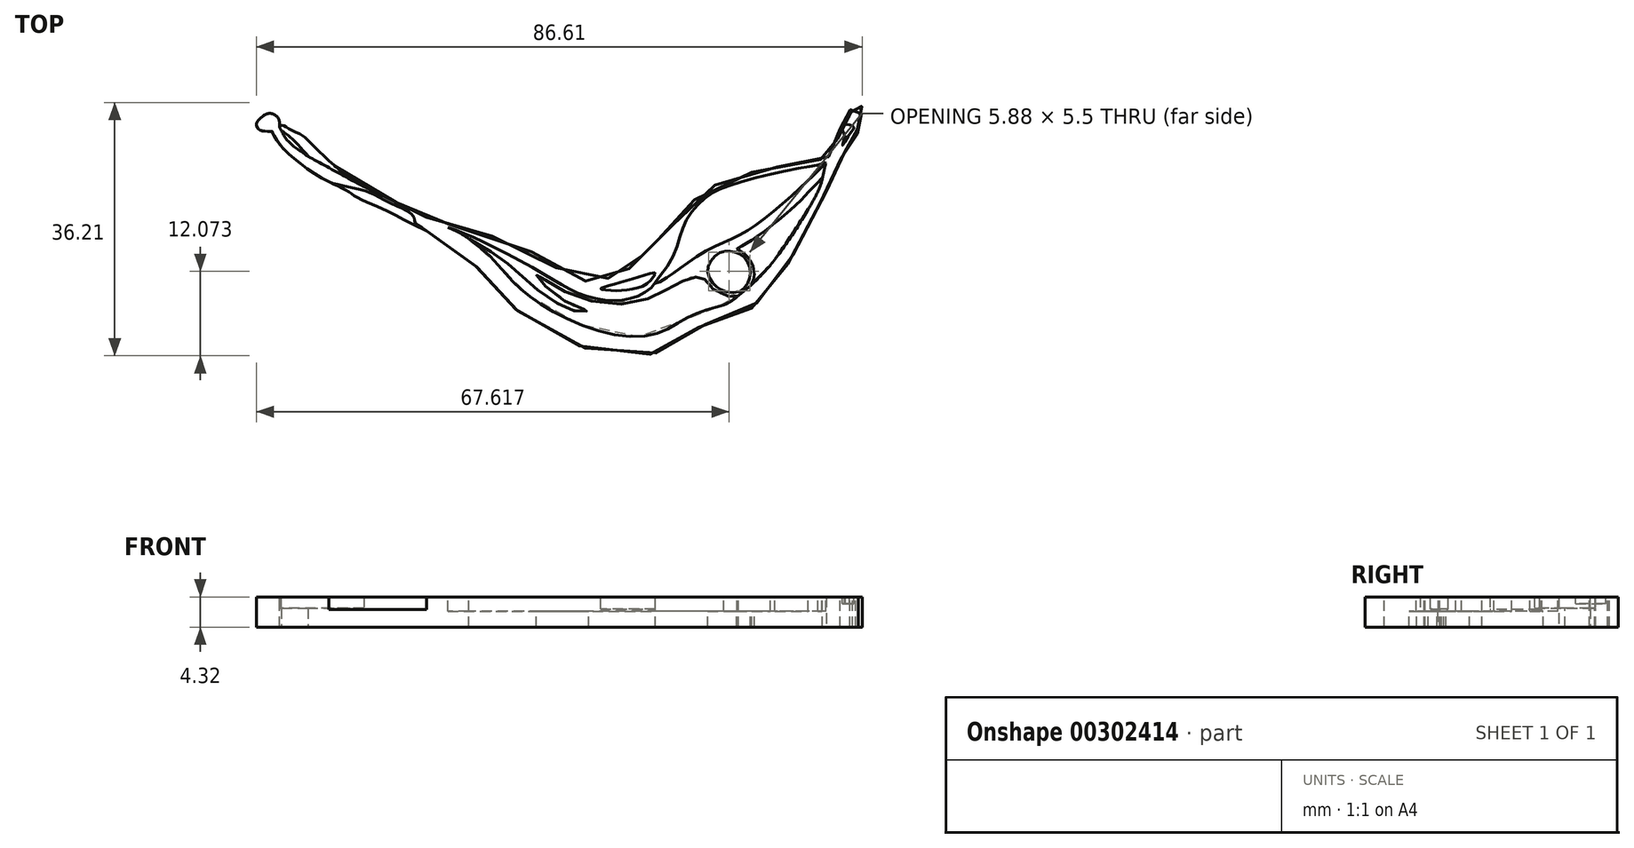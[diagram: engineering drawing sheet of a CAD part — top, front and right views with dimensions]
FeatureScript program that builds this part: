
annotation { "Feature Type Name" : "Feature", "Feature Type Description" : "" }
export const myFeature = defineFeature(function(context is Context, id is Id, definition is map)
    precondition{}
    {
        {
            var Q0;
            Q0=qCreatedBy(makeId("Top.planeOp"),FACE);
            var sketch = newSketch(context, id + "F0", { "sketchPlane" : qUnion([Q0])});
            skFitSpline(sketch, "E0", {"points": [v(-43.46, 14.38) * mm, v(-44.23, 13.82) * mm, v(-44.8, 13.18) * mm, v(-44.82, 12.68) * mm, v(-44.36, 12.07) * mm, v(-43.25, 11.92) * mm, v(-42.68, 11.9) * mm, v(-42.57, 11.9) * mm, v(-42.53, 11.75) * mm, v(-41.7, 10.3) * mm, v(-39.3, 7.87) * mm, v(-34.59, 4.74) * mm, v(-31.85, 3.4) * mm, v(-30.37, 2.4) * mm, v(-26.53, 0.67) * mm, v(-23.64, -0.81) * mm, v(-20.37, -2.4) * mm, v(-17.35, -4.13) * mm, v(-13.45, -7.38) * mm, v(-9.8, -11.5) * mm, v(-7.92, -13.38) * mm, v(-5.1, -15.68) * mm, v(2.66, -19.24) * mm, v(8.89, -20.2) * mm, v(13.19, -19.5) * mm, v(16.5, -17.42) * mm, v(19.24, -15.76) * mm, v(23.96, -14.69) * mm, v(26.11, -13.28) * mm, v(28.6, -10.38) * mm, v(30.9, -7.42) * mm, v(33.51, -2.7) * mm, v(36.14, 2.38) * mm, v(38, 6.37) * mm, v(38.5, 7.84) * mm, v(39, 8.38) * mm, v(39.55, 9.56) * mm, v(40.04, 10.09) * mm, v(40.35, 11.03) * mm, v(41.15, 11.69) * mm, v(41.15, 11.97) * mm, v(40.9, 12.98) * mm, v(40.84, 13.54) * mm, v(40.94, 13.74) * mm, v(41.47, 14.13) * mm, v(41.74, 14.96) * mm, v(41.54, 15.76) * mm, v(40.73, 16) * mm, v(40.18, 15.73) * mm, v(40, 15.17) * mm, v(40.25, 14.82) * mm, v(40.39, 14.68) * mm, v(39.83, 14.68) * mm, v(39.2, 13.81) * mm, v(38.64, 12.7) * mm, v(38.57, 11.58) * mm, v(37.8, 10.12) * mm, v(37.42, 9.29) * mm, v(37.15, 8.48) * mm, v(36.8, 8.2) * mm, v(36.24, 8) * mm, v(32.93, 7.44) * mm, v(26.45, 6.18) * mm, v(22.34, 5) * mm, v(18.2, 2.44) * mm, v(15.35, -0.53) * mm, v(13.74, -2.57) * mm, v(11.52, -4.5) * mm, v(10.67, -5.35) * mm, v(9.53, -6.82) * mm, v(7.86, -8.1) * mm, v(6.39, -8.84) * mm, v(3.57, -9.5) * mm, v(0.75, -9.15) * mm, v(-3.47, -6.61) * mm, v(-7.61, -4.31) * mm, v(-16.63, -1.54) * mm, v(-19.79, -0.7) * mm, v(-23.14, 0.88) * mm, v(-29.1, 3.83) * mm, v(-33.31, 6.66) * mm, v(-37.33, 10.5) * mm, v(-38.62, 11.54) * mm, v(-40.4, 12.37) * mm, v(-41.2, 12.78) * mm, v(-41.53, 12.66) * mm, v(-41.53, 12.96) * mm, v(-41.76, 13.84) * mm, v(-42.64, 14.43) * mm, v(-43.46, 14.38) * mm]});
            skFitSpline(sketch, "E1", {"points": [v(-14.45, -3.47) * mm, v(-11.98, -5.47) * mm, v(-8.6, -9.16) * mm, v(-4.78, -12.4) * mm, v(3.52, -16.48) * mm, v(11.92, -17.15) * mm, v(16.23, -15.05) * mm, v(20, -13.5) * mm, v(22.54, -12.67) * mm, v(23.7, -11.87) * mm, v(24.06, -11.6) * mm, v(23.7, -11.71) * mm, v(23.36, -11.76) * mm, v(22.28, -11.66) * mm, v(20.73, -10.86) * mm, v(19.84, -10.07) * mm, v(19.35, -9.27) * mm, v(19.1, -9.24) * mm, v(18.81, -9.13) * mm, v(18.34, -8.96) * mm, v(17.72, -8.93) * mm, v(16.78, -9.06) * mm, v(15.52, -9.94) * mm, v(13.74, -10.75) * mm, v(12.14, -11.6) * mm, v(9.16, -12.63) * mm, v(4.7, -12.7) * mm, v(0.45, -11.54) * mm, v(-2.41, -10.03) * mm, v(-4.02, -9.05) * mm, v(-4.68, -8.62) * mm, v(-4.8, -8.64) * mm, v(-4.78, -8.75) * mm, v(-4.2, -9.48) * mm, v(-3.27, -10.53) * mm, v(-0.57, -12.48) * mm, v(1.68, -13.47) * mm, v(2.44, -13.62) * mm, v(2.56, -13.66) * mm, v(2.63, -13.74) * mm, v(2.54, -13.8) * mm, v(2.23, -13.85) * mm, v(1.72, -13.87) * mm, v(0.62, -13.77) * mm, v(-0.47, -13.35) * mm, v(-2.89, -12.12) * mm, v(-5.08, -10.42) * mm, v(-6.62, -9.1) * mm, v(-7.7, -7.93) * mm, v(-9.64, -6.52) * mm, v(-11.55, -5.11) * mm, v(-14.45, -3.47) * mm]});
            skFitSpline(sketch, "E2", {"points": [v(12.2, -9.81) * mm, v(14.18, -7) * mm, v(15.74, -3.08) * mm, v(17.1, 0) * mm, v(19.55, 2.56) * mm, v(22.34, 4.02) * mm, v(30.1, 6.1) * mm, v(35.1, 7.05) * mm, v(36.11, 7.31) * mm, v(36.51, 7.45) * mm, v(36.62, 7.48) * mm, v(36.54, 7.38) * mm, v(35.62, 6.44) * mm, v(34.13, 5) * mm, v(30.47, 1.6) * mm, v(26.26, -1.68) * mm, v(23.17, -3.45) * mm, v(19.85, -4.99) * mm, v(15.96, -7.51) * mm, v(13.72, -9.06) * mm, v(12.2, -9.81) * mm]});
            skFitSpline(sketch, "E3", {"points": [v(23.8, -4.96) * mm, v(24.13, -5.1) * mm, v(25.71, -6.5) * mm, v(26.28, -8.03) * mm, v(26.22, -9.26) * mm, v(25.98, -9.9) * mm, v(26.37, -9.55) * mm, v(28.15, -7.77) * mm, v(29.91, -5.54) * mm, v(32.05, -2.29) * mm, v(34.42, 1.4) * mm, v(35.71, 3.98) * mm, v(36.04, 5.01) * mm, v(36.07, 5.2) * mm, v(36.07, 5.3) * mm, v(35.97, 5.22) * mm, v(35.8, 5.01) * mm, v(34.73, 3.9) * mm, v(32.75, 1.82) * mm, v(28.99, -1.45) * mm, v(27.07, -2.89) * mm, v(24.53, -4.52) * mm, v(23.8, -4.96) * mm]});
            skFitSpline(sketch, "E4", {"points": [v(23.56, -5.38) * mm, v(24.75, -5.97) * mm, v(25.7, -7.5) * mm, v(25.71, -8.83) * mm, v(25.2, -10.15) * mm, v(23.8, -11.15) * mm, v(21.76, -10.81) * mm, v(20.69, -10.11) * mm, v(19.78, -8.74) * mm, v(19.86, -7.13) * mm, v(21.02, -5.68) * mm, v(22.4, -5.25) * mm, v(23.56, -5.38) * mm]});
            skFitSpline(sketch, "E5", {"points": [v(-37.48, 8.36) * mm, v(-38.4, 9) * mm, v(-39.47, 9.7) * mm, v(-40.17, 10.38) * mm, v(-40.78, 11.08) * mm, v(-41.2, 11.88) * mm, v(-41.26, 11.99) * mm, v(-41.14, 11.94) * mm, v(-40.59, 11.5) * mm, v(-39.83, 10.94) * mm, v(-38.98, 10.06) * mm, v(-37.87, 8.86) * mm, v(-37.48, 8.36) * mm]});
            skSolve(sketch);
        }
        {
            var Q0;
            Q0=qSketchRegion(id+"F0",true);
            extrude(context, id + "F1", {"entities" : qUnion([Q0]), "depth" : 4.32 * mm});
        }
        {
            var Q0;
            Q0=makeQuery(id+"F1.opExtrude","CAP_FACE",FACE,{"disambiguationData":[OSD([sQuery(id+"F0.wireOp",EDGE,"E0"),sQuery(id+"F0.wireOp",EDGE,"E1"),sQuery(id+"F0.wireOp",EDGE,"E2"),sQuery(id+"F0.wireOp",EDGE,"E3"),sQuery(id+"F0.wireOp",EDGE,"E4"),sQuery(id+"F0.wireOp",EDGE,"E5")])],"isStart":false});
            var sketch = newSketch(context, id + "F2", { "sketchPlane" : qUnion([Q0])});
            skFitSpline(sketch, "E6", {"points": [v(-41.56, 12.7) * mm, v(-41.52, 12.46) * mm, v(-41.26, 11.98) * mm], "startDerivative": vector(0.03, -0.57) * mm, "endDerivative": vector(0.54, -0.86) * mm});
            skFitSpline(sketch, "E7", {"points": [v(-37.55, 8.4) * mm, v(-37.29, 8.23) * mm, v(-35.44, 7.23) * mm, v(-32.92, 5.83) * mm, v(-29.47, 4.04) * mm], "startDerivative": vector(1.64, -0.93) * mm, "endDerivative": vector(9.67, -4.78) * mm});
            skLineSegment(sketch, "E8", {"start": v(-41.56, 12.7) * mm, "end": v(-39.23, 15.85) * mm});
            skLineSegment(sketch, "E9", {"start": v(-39.23, 15.85) * mm, "end": v(-29.46, 12.02) * mm});
            skLineSegment(sketch, "E10", {"start": v(-29.46, 12.02) * mm, "end": v(-29.47, 4.04) * mm});
            skLineSegment(sketch, "E11", {"start": v(-41.26, 11.98) * mm, "end": v(-37.55, 8.4) * mm});
            skSolve(sketch);
        }
        {
            var Q0;
            Q0 = qSketchRegion(id + "F2", true);
            extrude(context, id + "F3", {"entities" : qUnion([Q0]), "operationType" : NewBodyOperationType.REMOVE, "oppositeDirection" : true, "depth" : 1.6 * mm});
        }
        {
            var Q0;
            Q0=makeQuery(id+"F1.opExtrude","CAP_FACE",FACE,{"disambiguationData":[OSD([sQuery(id+"F0.wireOp",EDGE,"E0"),sQuery(id+"F0.wireOp",EDGE,"E1"),sQuery(id+"F0.wireOp",EDGE,"E2"),sQuery(id+"F0.wireOp",EDGE,"E3"),sQuery(id+"F0.wireOp",EDGE,"E4"),sQuery(id+"F0.wireOp",EDGE,"E5")])],"isStart":false});
            var sketch = newSketch(context, id + "F4", { "sketchPlane" : qUnion([Q0])});
            skFitSpline(sketch, "E12", {"points": [v(-42.67, 11.63) * mm, v(-42.65, 12.53) * mm, v(-42.93, 13.46) * mm, v(-43.57, 13.78) * mm, v(-44.4, 13.24) * mm, v(-44.37, 12.49) * mm, v(-44.09, 12.19) * mm, v(-42.67, 11.63) * mm]});
            skSolve(sketch);
        }
        {
            var Q0;
            {var subQ0=sQuery(id+"F4.wireOp",EDGE,"E12");var subQ1=makeQuery(id+"F1.opExtrude","CAP_EDGE",EDGE,{"disambiguationData":[OSD([sQuery(id+"F0.wireOp",EDGE,"E0")])],"isStart":false});var subQ2=makeQuery(id+"F4.imprint","INTERSECT",VERTEX,{"disambiguationData":[OD(0.0)],"derivedFrom":[subQ1,subQ0]});Q0=makeQuery(id+"F4.imprint","IMPRINT",FACE,{"disambiguationData":[TD([[makeQuery(id+"F4.imprint","IMPRINT",EDGE,{"disambiguationData":[TD([[subQ2,-1.0]])],"derivedFrom":subQ0}),1.0]])]});}
            var Q1;
            Q1=sQuery(id+"F4.wireOp",EDGE,"E12");
            extrude(context, id + "F5", {"entities" : qUnion([Q0]), "operationType" : NewBodyOperationType.REMOVE, "surfaceEntities" : qUnion([Q1]), "oppositeDirection" : true, "depth" : 1.6 * mm});
        }
        {
            var Q0;
            Q0=makeQuery(id+"F1.opExtrude","CAP_FACE",FACE,{"disambiguationData":[OSD([sQuery(id+"F0.wireOp",EDGE,"E0"),sQuery(id+"F0.wireOp",EDGE,"E1"),sQuery(id+"F0.wireOp",EDGE,"E2"),sQuery(id+"F0.wireOp",EDGE,"E3"),sQuery(id+"F0.wireOp",EDGE,"E4"),sQuery(id+"F0.wireOp",EDGE,"E5")])],"isStart":false});
            var sketch = newSketch(context, id + "F6", { "sketchPlane" : qUnion([Q0])});
            skFitSpline(sketch, "E13", {"points": [v(-34.5, 4.7) * mm, v(-32.52, 4.14) * mm, v(-29.38, 3.41) * mm, v(-27.53, 2.59) * mm, v(-24.1, 0.92) * mm, v(-22.83, 0.25) * mm, v(-22.24, -0.62) * mm, v(-22.12, -1.15) * mm, v(-20.52, -2.32) * mm, v(-19.28, -3.42) * mm, v(-19.28, -3.67) * mm, v(-34.28, -4.1) * mm, v(-46.13, 8) * mm, v(-37.67, 6.07) * mm, v(-34.5, 4.7) * mm]});
            skSolve(sketch);
        }
        {
            var Q0;
            Q0 = qSketchRegion(id + "F6", true);
            extrude(context, id + "F7", {"entities" : qUnion([Q0]), "operationType" : NewBodyOperationType.REMOVE, "oppositeDirection" : true, "depth" : 1.78 * mm});
        }
        {
            var Q0;
            Q0=makeQuery(id+"F1.opExtrude","CAP_FACE",FACE,{"disambiguationData":[OSD([sQuery(id+"F0.wireOp",EDGE,"E0"),sQuery(id+"F0.wireOp",EDGE,"E1"),sQuery(id+"F0.wireOp",EDGE,"E2"),sQuery(id+"F0.wireOp",EDGE,"E3"),sQuery(id+"F0.wireOp",EDGE,"E4"),sQuery(id+"F0.wireOp",EDGE,"E5")])],"isStart":false});
            var sketch = newSketch(context, id + "F8", { "sketchPlane" : qUnion([Q0])});
            skFitSpline(sketch, "E14", {"points": [v(-14.45, -3.48) * mm, v(-15.83, -2.58) * mm, v(-17.5, -1.8) * mm, v(-19.84, -0.68) * mm], "startDerivative": vector(-4.45, 3.12) * mm, "endDerivative": vector(-6.33, 3.33) * mm});
            skFitSpline(sketch, "E15", {"points": [v(-17.5, -1.8) * mm, v(-12.53, -3.83) * mm, v(-3.37, -8.75) * mm, v(1.33, -11.3) * mm, v(6.19, -12.3) * mm, v(10, -11.52) * mm, v(12.26, -9.59) * mm], "startDerivative": vector(26.31, -9.77) * mm, "endDerivative": vector(8.56, 17.9) * mm});
            skFitSpline(sketch, "E16", {"points": [v(12.26, -9.59) * mm, v(17.9, -3.92) * mm, v(27.08, 3.73) * mm, v(33.87, 5.94) * mm, v(36.55, 7.4) * mm], "startDerivative": vector(19.72, 19.82) * mm, "endDerivative": vector(14.32, 9.64) * mm});
            skFitSpline(sketch, "E17", {"points": [v(36.55, 7.4) * mm, v(36.06, 5.08) * mm, v(35.44, 3.35) * mm, v(28.6, -7.26) * mm, v(23.84, -11.77) * mm, v(21.96, -12.91) * mm, v(16.18, -13.7) * mm, v(5.65, -15.28) * mm, v(-1.48, -13.62) * mm, v(-8.37, -8.4) * mm, v(-12.04, -5.07) * mm, v(-14.45, -3.48) * mm], "startDerivative": vector(-8.87, -42.52) * mm, "endDerivative": vector(-36.1, 21.51) * mm});
            skSolve(sketch);
        }
        {
            var Q0;
            Q0 = qSketchRegion(id + "F8", true);
            var Q1;
            Q1=makeQuery(id+"F8.imprint","IMPRINT",FACE,{"disambiguationData":[TD([[makeQuery(id+"F8.imprint","IMPRINT",EDGE,{"derivedFrom":makeQuery(id+"F1.opExtrude","CAP_EDGE",EDGE,{"disambiguationData":[OSD([sQuery(id+"F0.wireOp",EDGE,"E4")])],"isStart":false})}),-1.0]])]});
            extrude(context, id + "F9", {"entities" : qUnion([Q0, Q1]), "operationType" : NewBodyOperationType.REMOVE, "oppositeDirection" : true, "depth" : 2.06 * mm});
        }
        {
            var Q0;
            Q0=makeQuery(id+"F1.opExtrude","CAP_FACE",FACE,{"disambiguationData":[OSD([sQuery(id+"F0.wireOp",EDGE,"E0"),sQuery(id+"F0.wireOp",EDGE,"E1"),sQuery(id+"F0.wireOp",EDGE,"E2"),sQuery(id+"F0.wireOp",EDGE,"E3"),sQuery(id+"F0.wireOp",EDGE,"E4"),sQuery(id+"F0.wireOp",EDGE,"E5")])],"isStart":false});
            var sketch = newSketch(context, id + "F10", { "sketchPlane" : qUnion([Q0])});
            skFitSpline(sketch, "E18", {"points": [v(6.6, -10.89) * mm, v(8.28, -10.74) * mm, v(10.11, -10.37) * mm, v(11.34, -9.58) * mm, v(12.17, -8.38) * mm, v(10.78, -8.6) * mm, v(8.65, -9.28) * mm, v(6.3, -9.95) * mm, v(4.95, -10.36) * mm, v(4.35, -10.62) * mm, v(4.95, -10.77) * mm, v(6.6, -10.89) * mm]});
            skSolve(sketch);
        }
        {
            var Q0;
            Q0 = qSketchRegion(id + "F10", true);
            extrude(context, id + "F11", {"entities" : qUnion([Q0]), "operationType" : NewBodyOperationType.REMOVE, "oppositeDirection" : true, "depth" : 1.75 * mm});
        }
        {
            var Q0;
            Q0=makeQuery(id+"F1.opExtrude","CAP_FACE",FACE,{"disambiguationData":[OSD([sQuery(id+"F0.wireOp",EDGE,"E0"),sQuery(id+"F0.wireOp",EDGE,"E1"),sQuery(id+"F0.wireOp",EDGE,"E2"),sQuery(id+"F0.wireOp",EDGE,"E3"),sQuery(id+"F0.wireOp",EDGE,"E4"),sQuery(id+"F0.wireOp",EDGE,"E5")])],"isStart":false});
            var sketch = newSketch(context, id + "F12", { "sketchPlane" : qUnion([Q0])});
            skFitSpline(sketch, "E19", {"points": [v(39.96, 14.24) * mm, v(39.62, 13.62) * mm, v(39.4, 12.95) * mm, v(40.27, 12.76) * mm, v(40.6, 12.4) * mm, v(40.02, 11.62) * mm, v(38.95, 9.9) * mm, v(39.22, 11) * mm, v(39.04, 11.87) * mm, v(38.9, 12.58) * mm, v(39.2, 13.44) * mm, v(39.96, 14.24) * mm]});
            skSolve(sketch);
        }
        {
            var Q0;
            Q0=makeQuery(id+"F12.imprint","IMPRINT",FACE,{"disambiguationData":[TD([[makeQuery(id+"F12.imprint","IMPRINT",EDGE,{"derivedFrom":sQuery(id+"F12.wireOp",EDGE,"E19")}),-1.0]])]});
            extrude(context, id + "F13", {"entities" : qUnion([Q0]), "operationType" : NewBodyOperationType.REMOVE, "oppositeDirection" : true, "depth" : 0.94 * mm});
        }
    });
